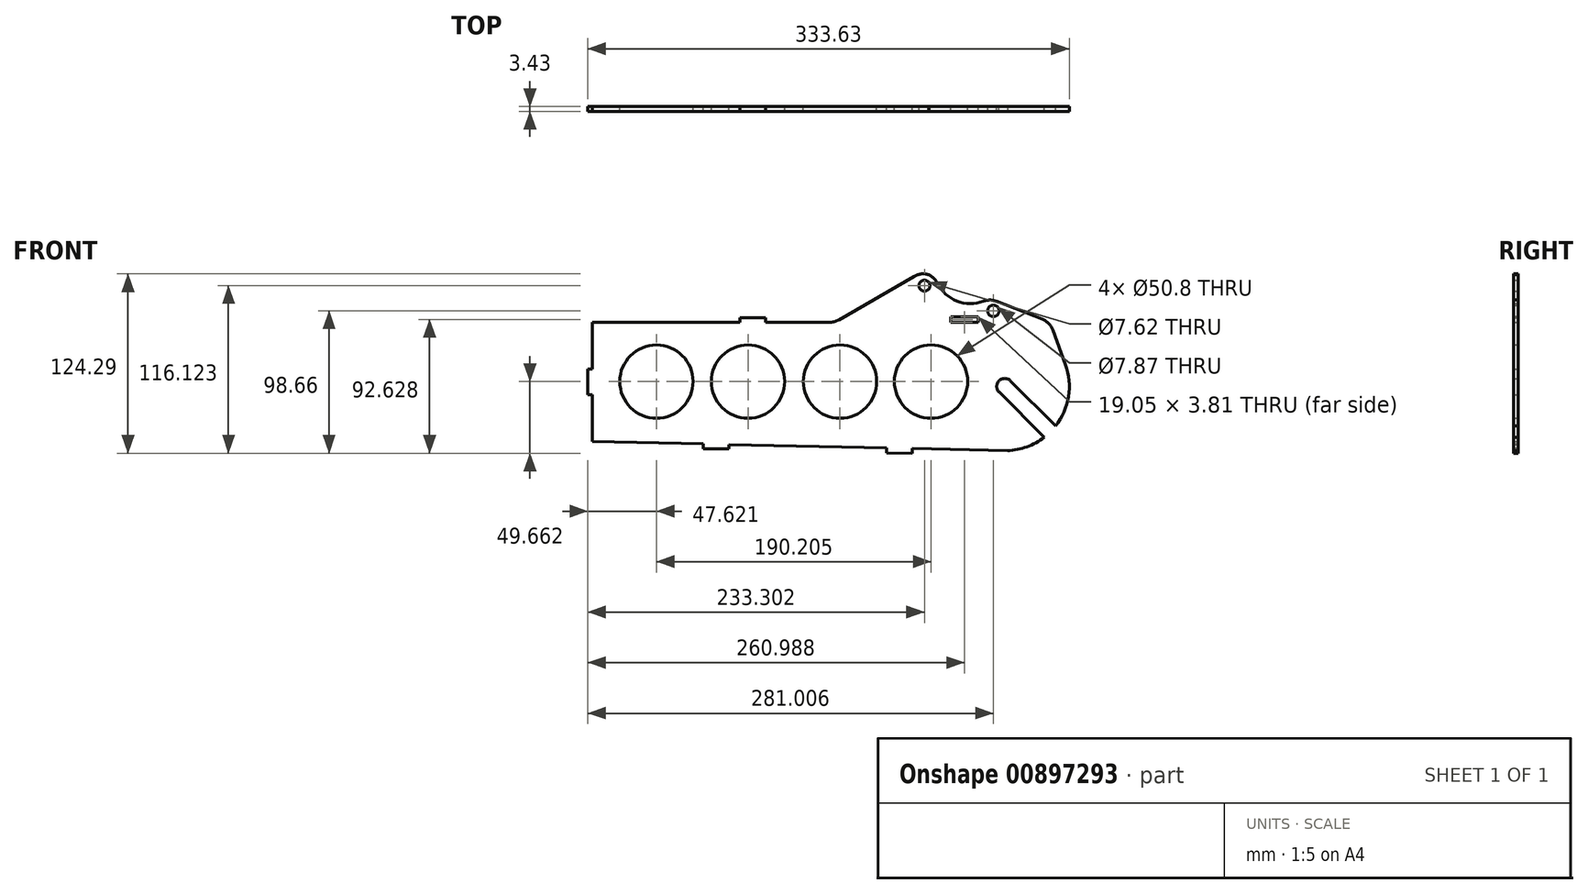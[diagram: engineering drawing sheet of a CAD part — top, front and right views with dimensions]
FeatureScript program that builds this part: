
annotation { "Feature Type Name" : "Feature", "Feature Type Description" : "" }
export const myFeature = defineFeature(function(context is Context, id is Id, definition is map)
    precondition{}
    {
        {
            var Q0;
            Q0=qCreatedBy(makeId("Front.planeOp"),FACE);
            var sketch = newSketch(context, id + "F0", { "sketchPlane" : qUnion([Q0])});
            skCircle(sketch, "E0", {"center": v(356.23, 242.4) * mm, "radius": 3.81 * mm});
            skCircle(sketch, "E1", {"center": v(403.94, 224.93) * mm, "radius": 3.94 * mm});
            skLineSegment(sketch, "E2", {"start": v(126.1, 166.83) * mm, "end": v(126.1, 134.44) * mm});
            skLineSegment(sketch, "E3", {"start": v(122.93, 166.83) * mm, "end": v(126.1, 166.83) * mm});
            skLineSegment(sketch, "E4", {"start": v(122.93, 184.6) * mm, "end": v(122.93, 166.83) * mm});
            skLineSegment(sketch, "E5", {"start": v(126.1, 184.6) * mm, "end": v(122.93, 184.6) * mm});
            skLineSegment(sketch, "E6", {"start": v(126.1, 217) * mm, "end": v(126.1, 184.6) * mm});
            skLineSegment(sketch, "E7", {"start": v(228.34, 217) * mm, "end": v(126.1, 217) * mm});
            skLineSegment(sketch, "E8", {"start": v(228.34, 217) * mm, "end": v(228.34, 220.17) * mm});
            skLineSegment(sketch, "E9", {"start": v(228.34, 220.17) * mm, "end": v(246.12, 220.17) * mm});
            skLineSegment(sketch, "E10", {"start": v(246.12, 220.17) * mm, "end": v(246.12, 217) * mm});
            skLineSegment(sketch, "E11", {"start": v(290.44, 217) * mm, "end": v(246.12, 217) * mm});
            skArc(sketch, "E12", {"start": v(290.44, 217) * mm, "mid": v(293.73, 217.43) * mm, "end": v(296.8, 218.7) * mm});
            skLineSegment(sketch, "E13", {"start": v(349.04, 248.86) * mm, "end": v(296.8, 218.7) * mm});
            skArc(sketch, "E14", {"start": v(359.23, 249.96) * mm, "mid": v(354.02, 250.49) * mm, "end": v(349.04, 248.86) * mm});
            skArc(sketch, "E15", {"start": v(365.21, 244.08) * mm, "mid": v(362.72, 247.53) * mm, "end": v(359.23, 249.96) * mm});
            skArc(sketch, "E16", {"start": v(365.21, 244.08) * mm, "mid": v(378.71, 231.65) * mm, "end": v(397.07, 231.57) * mm});
            skArc(sketch, "E17", {"start": v(406.25, 231.52) * mm, "mid": v(401.66, 232.4) * mm, "end": v(397.07, 231.57) * mm});
            skLineSegment(sketch, "E18", {"start": v(437.9, 219.09) * mm, "end": v(406.25, 231.52) * mm});
            skArc(sketch, "E19", {"start": v(445.2, 211.61) * mm, "mid": v(442.35, 216.13) * mm, "end": v(437.9, 219.09) * mm});
            skLineSegment(sketch, "E20", {"start": v(453.88, 187.75) * mm, "end": v(445.2, 211.61) * mm});
            skArc(sketch, "E21", {"start": v(447.11, 145.14) * mm, "mid": v(456.01, 165.57) * mm, "end": v(453.88, 187.75) * mm});
            skLineSegment(sketch, "E22", {"start": v(447.11, 145.14) * mm, "end": v(415.79, 176.47) * mm});
            skArc(sketch, "E23", {"start": v(415.79, 176.47) * mm, "mid": v(407.93, 176.47) * mm, "end": v(407.93, 168.61) * mm});
            skLineSegment(sketch, "E24", {"start": v(407.93, 168.61) * mm, "end": v(439.22, 137.32) * mm});
            skArc(sketch, "E25", {"start": v(413.82, 128.13) * mm, "mid": v(427.24, 130.74) * mm, "end": v(439.22, 137.32) * mm});
            skLineSegment(sketch, "E26", {"start": v(347.85, 129.57) * mm, "end": v(413.82, 128.13) * mm});
            skLineSegment(sketch, "E27", {"start": v(347.78, 126.27) * mm, "end": v(347.85, 129.57) * mm});
            skLineSegment(sketch, "E28", {"start": v(330.07, 126.66) * mm, "end": v(347.78, 126.27) * mm});
            skLineSegment(sketch, "E29", {"start": v(330.07, 129.96) * mm, "end": v(330.07, 126.66) * mm});
            skLineSegment(sketch, "E30", {"start": v(220.6, 132.37) * mm, "end": v(330.07, 129.96) * mm});
            skLineSegment(sketch, "E31", {"start": v(220.6, 129.46) * mm, "end": v(220.6, 132.37) * mm});
            skLineSegment(sketch, "E32", {"start": v(202.82, 129.46) * mm, "end": v(220.6, 129.46) * mm});
            skLineSegment(sketch, "E33", {"start": v(202.82, 132.76) * mm, "end": v(202.82, 129.46) * mm});
            skLineSegment(sketch, "E34", {"start": v(126.1, 134.44) * mm, "end": v(202.82, 132.76) * mm});
            skLineSegment(sketch, "E35", {"start": v(393.44, 217) * mm, "end": v(393.44, 220.8) * mm});
            skLineSegment(sketch, "E36", {"start": v(393.44, 220.8) * mm, "end": v(374.4, 220.8) * mm});
            skLineSegment(sketch, "E37", {"start": v(374.4, 220.8) * mm, "end": v(374.4, 217) * mm});
            skLineSegment(sketch, "E38", {"start": v(374.4, 217) * mm, "end": v(393.44, 217) * mm});
            skCircle(sketch, "E39", {"center": v(170.55, 175.93) * mm, "radius": 25.4 * mm});
            skCircle(sketch, "E40", {"center": v(233.98, 175.93) * mm, "radius": 25.4 * mm});
            skCircle(sketch, "E41", {"center": v(297.72, 175.93) * mm, "radius": 25.4 * mm});
            skCircle(sketch, "E42", {"center": v(360.76, 175.93) * mm, "radius": 25.4 * mm});
            skSolve(sketch);
        }
        {
            var Q0;
            Q0 = qSketchRegion(id + "F0", true);
            extrude(context, id + "F1", {"entities" : qUnion([Q0]), "depth" : 3.43 * mm, "offsetDistance" : 25.4 * mm});
        }
    });
